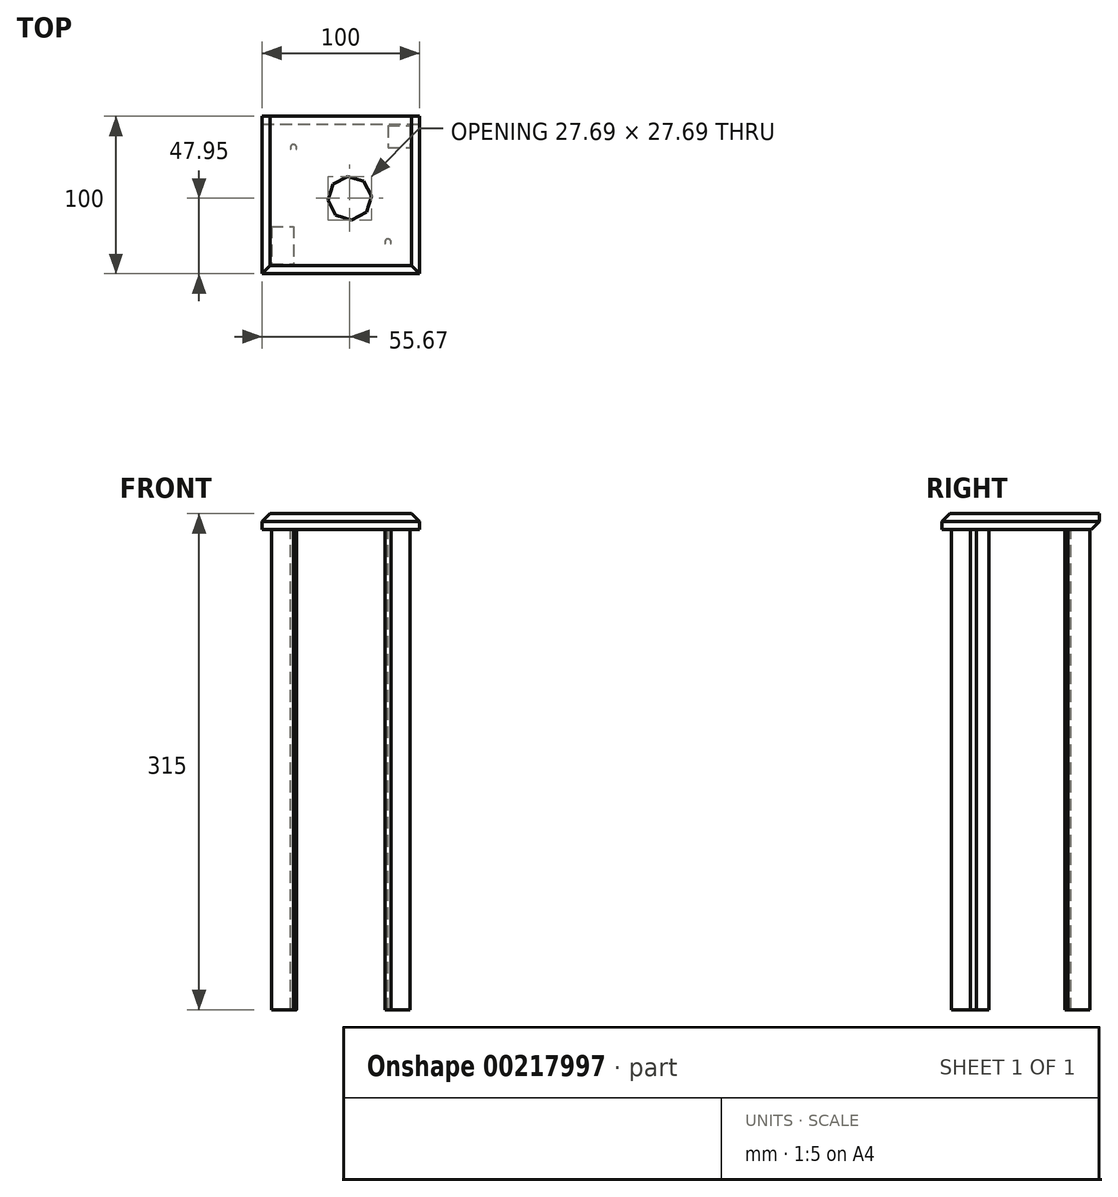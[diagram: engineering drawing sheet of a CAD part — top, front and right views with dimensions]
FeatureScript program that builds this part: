
annotation { "Feature Type Name" : "Feature", "Feature Type Description" : "" }
export const myFeature = defineFeature(function(context is Context, id is Id, definition is map)
    precondition{}
    {
        {
            var Q0;
            Q0=qCreatedBy(makeId("Top.planeOp"),FACE);
            var sketch = newSketch(context, id + "F0", { "sketchPlane" : qUnion([Q0])});
            skLineSegment(sketch, "E0.bottom", {"start": v(-55.67, 52.05) * mm, "end": v(44.33, 52.05) * mm});
            skLineSegment(sketch, "E0.top", {"start": v(-55.67, -47.95) * mm, "end": v(44.33, -47.95) * mm});
            skLineSegment(sketch, "E0.left", {"start": v(-55.67, 52.05) * mm, "end": v(-55.67, -47.95) * mm});
            skLineSegment(sketch, "E0.right", {"start": v(44.33, 52.05) * mm, "end": v(44.33, -47.95) * mm});
            skSolve(sketch);
        }
        {
            var Q0;
            Q0 = qSketchRegion(id + "F0", true);
            extrude(context, id + "F1", {"entities" : qUnion([Q0]), "depth" : 10 * mm});
        }
        {
            var Q0;
            Q0=qCreatedBy(makeId("Top.planeOp"),FACE);
            var sketch = newSketch(context, id + "F2", { "sketchPlane" : qUnion([Q0])});
            skCircle(sketch, "E1.cCircle", {"center": v(0, 0) * mm, "radius": 12.85 * mm, "construction": true});
            skLineSegment(sketch, "E1.0", {"start": v(1.3, -13.85) * mm, "end": v(-8.87, -10.71) * mm});
            skLineSegment(sketch, "E1.1", {"start": v(-8.87, -10.71) * mm, "end": v(-13.85, -1.3) * mm});
            skLineSegment(sketch, "E1.2", {"start": v(-13.85, -1.3) * mm, "end": v(-10.71, 8.87) * mm});
            skLineSegment(sketch, "E1.3", {"start": v(-10.71, 8.87) * mm, "end": v(-1.3, 13.85) * mm});
            skLineSegment(sketch, "E1.4", {"start": v(-1.3, 13.85) * mm, "end": v(8.87, 10.71) * mm});
            skLineSegment(sketch, "E1.5", {"start": v(8.87, 10.71) * mm, "end": v(13.85, 1.3) * mm});
            skLineSegment(sketch, "E1.6", {"start": v(13.85, 1.3) * mm, "end": v(10.71, -8.87) * mm});
            skLineSegment(sketch, "E1.7", {"start": v(10.71, -8.87) * mm, "end": v(1.3, -13.85) * mm});
            skPoint(sketch, "E1.0.midPoint", {"position": v(-3.78, -12.28) * mm});
            skSolve(sketch);
        }
        {
            var Q0;
            Q0=makeQuery(id+"F2.imprint","IMPRINT",FACE,{"disambiguationData":[TD([[makeQuery(id+"F2.imprint","IMPRINT",EDGE,{"derivedFrom":sQuery(id+"F2.wireOp",EDGE,"E1.0")}),-1.0]])]});
            extrude(context, id + "F3", {"entities" : qUnion([Q0]), "operationType" : NewBodyOperationType.REMOVE, "depth" : 28 * mm});
        }
        {
            var Q0;
            Q0=qCreatedBy(makeId("Top.planeOp"),FACE);
            var sketch = newSketch(context, id + "F4", { "sketchPlane" : qUnion([Q0])});
            skCircle(sketch, "E2", {"center": v(24.33, -27.95) * mm, "radius": 2 * mm});
            skSolve(sketch);
        }
        {
            var Q0;
            Q0=makeQuery(id+"F4.imprint","IMPRINT",FACE,{"disambiguationData":[TD([[makeQuery(id+"F4.imprint","IMPRINT",EDGE,{"derivedFrom":sQuery(id+"F4.wireOp",EDGE,"E2")}),1.0]])]});
            extrude(context, id + "F5", {"entities" : qUnion([Q0]), "operationType" : NewBodyOperationType.ADD, "oppositeDirection" : true, "depth" : 305 * mm});
        }
        {
            var Q0;
            Q0=qCreatedBy(makeId("Top.planeOp"),FACE);
            var sketch = newSketch(context, id + "F6", { "sketchPlane" : qUnion([Q0])});
            skCircle(sketch, "E3", {"center": v(-35.67, 32.05) * mm, "radius": 2 * mm});
            skSolve(sketch);
        }
        {
            var Q0;
            Q0=makeQuery(id+"F6.imprint","IMPRINT",FACE,{"disambiguationData":[TD([[makeQuery(id+"F6.imprint","IMPRINT",EDGE,{"derivedFrom":sQuery(id+"F6.wireOp",EDGE,"E3")}),1.0]])]});
            extrude(context, id + "F7", {"entities" : qUnion([Q0]), "operationType" : NewBodyOperationType.ADD, "oppositeDirection" : true, "depth" : 305 * mm});
        }
        {
            var Q0;
            Q0=qCreatedBy(makeId("Top.planeOp"),FACE);
            var sketch = newSketch(context, id + "F8", { "sketchPlane" : qUnion([Q0])});
            skLineSegment(sketch, "E4.bottom", {"start": v(-49.67, -17.95) * mm, "end": v(-35.67, -17.95) * mm});
            skLineSegment(sketch, "E4.top", {"start": v(-49.67, -41.95) * mm, "end": v(-35.67, -41.95) * mm});
            skLineSegment(sketch, "E4.left", {"start": v(-49.67, -17.95) * mm, "end": v(-49.67, -41.95) * mm});
            skLineSegment(sketch, "E4.right", {"start": v(-35.67, -17.95) * mm, "end": v(-35.67, -41.95) * mm});
            skLineSegment(sketch, "E5.bottom", {"start": v(24.33, 46.05) * mm, "end": v(38.33, 46.05) * mm});
            skLineSegment(sketch, "E5.top", {"start": v(24.33, 32.05) * mm, "end": v(38.33, 32.05) * mm});
            skLineSegment(sketch, "E5.left", {"start": v(24.33, 46.05) * mm, "end": v(24.33, 32.05) * mm});
            skLineSegment(sketch, "E5.right", {"start": v(38.33, 46.05) * mm, "end": v(38.33, 32.05) * mm});
            skSolve(sketch);
        }
        {
            var Q0;
            Q0=makeQuery(id+"F8.imprint","IMPRINT",FACE,{"disambiguationData":[TD([[makeQuery(id+"F8.imprint","IMPRINT",EDGE,{"derivedFrom":sQuery(id+"F8.wireOp",EDGE,"E4.bottom")}),-1.0]])]});
            var Q1;
            Q1=makeQuery(id+"F8.imprint","IMPRINT",FACE,{"disambiguationData":[TD([[makeQuery(id+"F8.imprint","IMPRINT",EDGE,{"derivedFrom":sQuery(id+"F8.wireOp",EDGE,"E5.bottom")}),-1.0]])]});
            extrude(context, id + "F9", {"entities" : qUnion([Q0, Q1]), "operationType" : NewBodyOperationType.ADD, "oppositeDirection" : true, "depth" : 305 * mm});
        }
        {
            var Q0;
            Q0=makeQuery(id+"F1.opExtrude","CAP_EDGE",EDGE,{"disambiguationData":[OSD([sQuery(id+"F0.wireOp",EDGE,"E0.left")])],"isStart":false});
            var Q1;
            Q1=makeQuery(id+"F1.opExtrude","CAP_EDGE",EDGE,{"disambiguationData":[OSD([sQuery(id+"F0.wireOp",EDGE,"E0.top")])],"isStart":false});
            var Q2;
            Q2=makeQuery(id+"F1.opExtrude","CAP_EDGE",EDGE,{"disambiguationData":[OSD([sQuery(id+"F0.wireOp",EDGE,"E0.bottom")])],"isStart":true});
            var Q3;
            Q3=makeQuery(id+"F1.opExtrude","CAP_EDGE",EDGE,{"disambiguationData":[OSD([sQuery(id+"F0.wireOp",EDGE,"E0.right")])],"isStart":false});
            chamfer(context, id + "F10", {"entities" : qUnion([Q0, Q1, Q2, Q3]), "width" : 5 * mm, "tangentPropagation" : true});
        }
    });
